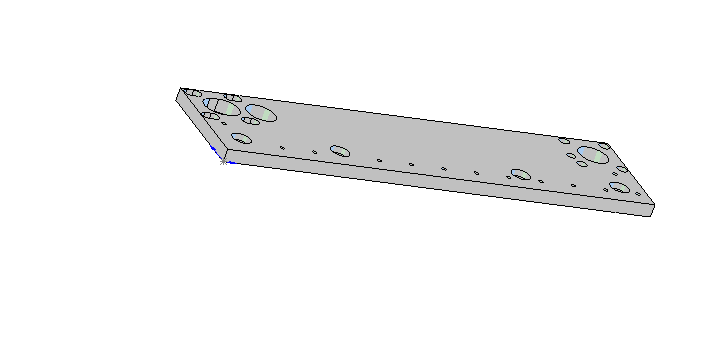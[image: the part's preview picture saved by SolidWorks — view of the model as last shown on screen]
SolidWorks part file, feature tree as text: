
SOLIDWORKS PART (.sldprt)
format: sldprt  version: not decoded by parser v0  size: 475,648 bytes
history: native  units: mm
features: sketch x5, cut_extrude x4, extrude x1 + 1 further entry (+10 scaffold rows collapsed)
feature tree (21):
  "Annotations"  RD1=6.4516mm RD2=9.525mm
  scaffold x10  (default folders/planes/origin — collapsed)
  sketch  "Sketch1"  dims[D7=12.7mm D1=82.55mm D2=330.2mm D3=38.1mm D4=38.1mm D5=38.1mm D6=38.1mm]
  extrude  "Extrude1"  Depth=9.525mm
  sketch  "Sketch2"  dims[c1.D1=22.098mm c1.D2=22.098mm c1.D4=22.098mm c1.D7=3.175mm c1.D8=3.175mm c1.D9=22.0mm c1.D10=3.175mm c1.D12=3.175mm c1.D14=22.098mm c1.D15=22.098mm c2.D7=3.175mm c2.D12=3.175mm c2.D13=3.175mm c2.D16=3.175mm c2.D10=6.35mm c3.D16=22.098mm c3.D17=3.81mm c3.D12=3.175mm c3.D21=7.9375mm c3.D22=7.9375mm c3.D23=~10.520232mm c3.D24=~10.520232mm c3.D25=7.9375mm c3.D26=7.9375mm c3.D27=22.098mm c3.D28=22.098mm c3.D31=22.098mm c3.D32=3.175mm c3.D33=22.098mm c3.D34=22.098mm c3.D35=22.098mm c3.D36=22.098mm c3.D37=3.175mm c3.D38=3.175mm c3.D39=3.175mm c3.D40=3.175mm c3.D41=3.175mm c3.D42=3.175mm c3.D43=22.0mm c3.D44=22.0mm c4.D43=11.0mm c4.D2=20.32mm c4.D3=20.32mm c4.D5=20.32mm c4.D6=20.32mm c4.D11=38.1mm c4.D12=19.05mm c4.D13=19.05mm c4.D14=32.258mm c4.D15=1.651mm c5.D12=19.05mm c5.D13=6.35mm c5.D16=19.05mm c5.D17=25.4mm c6.D12=6.35mm c6.D18=19.05mm c6.D19=19.05mm c6.D20=19.05mm c6.D23=95.25mm c6.D24=95.25mm c6.D27=15.5mm c6.D28=15.494mm c6.D29=15.494mm c6.D30=~49.945697mm c6.D31=15.494mm c6.D33=15.494mm c6.D34=15.494mm c6.D35=15.494mm c6.D36=15.494mm c6.D39=5.08mm c6.D40=5.08mm c6.D41=5.08mm c6.D42=5.08mm c6.D44=5.08mm]
  cut_extrude  "Cut-Extrude1"  [1 undecoded]
  sketch  "Sketch3"  dims[D1=13.97mm]
  cut_extrude  "Cut-Extrude2"  Depth=4.572mm
  sketch  "Sketch4"  dims[c1.D3=3.175mm c1.D4=3.175mm c1.D5=3.175mm c1.D6=3.175mm c1.D7=3.175mm c1.D8=3.175mm c1.D9=3.175mm c1.D10=3.175mm c1.D11=3.175mm c1.D12=3.175mm c1.D13=3.175mm c1.D14=3.175mm c1.D15=3.175mm c1.D16=3.175mm c2.D13=3.175mm c2.D17=3.175mm c2.D12=3.175mm c3.D13=3.175mm c3.D1=12.7mm c3.D2=7.493mm c3.D4=24.9936mm c3.D5=24.9936mm c3.D6=24.9936mm c3.D7=24.9936mm c3.D8=24.9936mm c3.D9=24.9936mm c3.D10=24.9936mm c3.D11=24.9936mm c3.D12=24.9936mm c4.D13=24.9936mm c4.D14=24.9936mm c4.D15=24.9936mm c4.D16=299.9232mm c5.D13=49.9872mm c5.D12=49.9872mm]
  cut_extrude  "Cut-Extrude3"  [1 undecoded]
  sketch  "Sketch6"  dims[c1.D1=7.62mm c1.D2=5.08mm c1.D3=5.08mm c2.D1=2.54mm c2.D2=2.54mm c2.D3=2.54mm c2.D4=2.54mm]
  cut_extrude  "Cut-Extrude4"  Depth=6.4516mm
decode coverage: 8 of 10 modeling features carry decoded parameters; 1 rows unclassified (native names shown)
note: ~ marks probable driven/reference dimensions
note: 2 parameter values undecoded
note: suppression state not decoded; provenance and decode notes live in map.json
